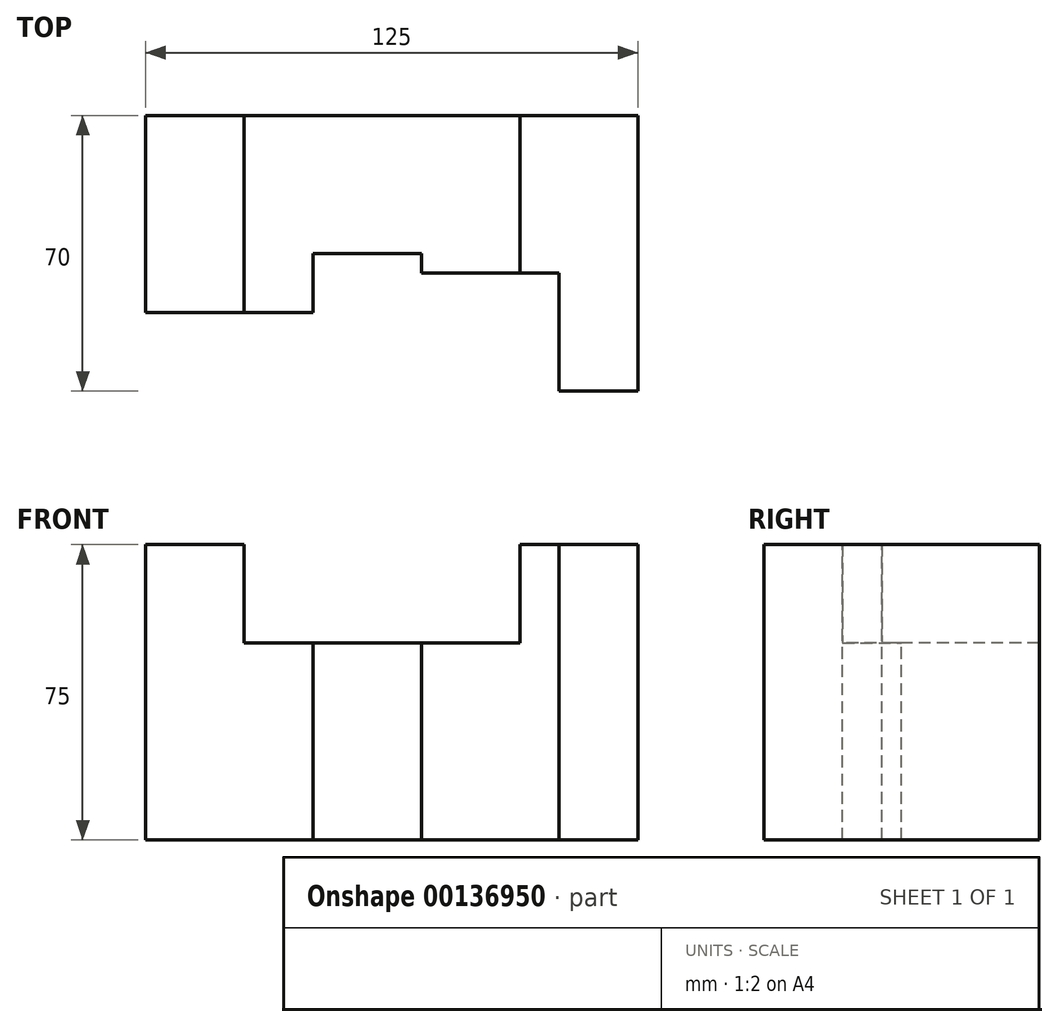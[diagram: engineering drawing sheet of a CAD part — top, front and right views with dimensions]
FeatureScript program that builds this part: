
annotation { "Feature Type Name" : "Feature", "Feature Type Description" : "" }
export const myFeature = defineFeature(function(context is Context, id is Id, definition is map)
    precondition{}
    {
        {
            var Q0;
            Q0=qCreatedBy(makeId("Right.planeOp"),FACE);
            var sketch = newSketch(context, id + "F0", { "sketchPlane" : qUnion([Q0])});
            skLineSegment(sketch, "E0.bottom", {"start": v(0, 0) * mm, "end": v(70, 0) * mm});
            skLineSegment(sketch, "E0.top", {"start": v(0, 75) * mm, "end": v(70, 75) * mm});
            skLineSegment(sketch, "E0.left", {"start": v(0, 0) * mm, "end": v(0, 75) * mm});
            skLineSegment(sketch, "E0.right", {"start": v(70, 0) * mm, "end": v(70, 75) * mm});
            skSolve(sketch);
        }
        {
            var Q0;
            Q0 = qSketchRegion(id + "F0", true);
            extrude(context, id + "F1", {"entities" : qUnion([Q0]), "depth" : 125 * mm});
        }
        {
            var Q0;
            Q0=makeQuery(id+"F1.opExtrude","SWEPT_FACE",FACE,{"disambiguationData":[OSD([sQuery(id+"F0.wireOp",EDGE,"E0.top")])]});
            var sketch = newSketch(context, id + "F2", { "sketchPlane" : qUnion([Q0])});
            skLineSegment(sketch, "E1.0.0", {"start": v(0, 70) * mm, "end": v(0, 0) * mm});
            skLineSegment(sketch, "E1.0.1", {"start": v(0, 0) * mm, "end": v(125, 0) * mm});
            skLineSegment(sketch, "E1.0.2", {"start": v(125, 0) * mm, "end": v(125, 70) * mm});
            skLineSegment(sketch, "E1.0.3", {"start": v(125, 70) * mm, "end": v(0, 70) * mm});
            skLineSegment(sketch, "E2", {"start": v(0, 20) * mm, "end": v(42.5, 20) * mm});
            skLineSegment(sketch, "E3", {"start": v(42.5, 20) * mm, "end": v(42.5, 35) * mm});
            skLineSegment(sketch, "E4", {"start": v(42.5, 35) * mm, "end": v(70, 35) * mm});
            skLineSegment(sketch, "E5", {"start": v(70, 35) * mm, "end": v(70, 30) * mm});
            skLineSegment(sketch, "E6", {"start": v(70, 30) * mm, "end": v(105, 30) * mm});
            skLineSegment(sketch, "E7", {"start": v(105, 30) * mm, "end": v(105, 0) * mm});
            skSolve(sketch);
        }
        {
            var Q0;
            {var subQ0=sQuery(id+"F2.wireOp",EDGE,"E2");Q0=makeQuery(id+"F2.imprint","IMPRINT",FACE,{"disambiguationData":[TD([[makeQuery(id+"F2.imprint","IMPRINT",EDGE,{"derivedFrom":subQ0}),-1.0]])]});}
            extrude(context, id + "F3", {"entities" : qUnion([Q0]), "operationType" : NewBodyOperationType.REMOVE, "endBound" : BoundingType.THROUGH_ALL, "oppositeDirection" : true, "depth" : 25 * mm});
        }
        {
            var Q0;
            Q0=makeQuery(id+"F3.boolean.opBoolean","COPY",FACE,{"derivedFrom":makeQuery(id+"F3.opExtrude","SWEPT_FACE",FACE,{"disambiguationData":[OSD([sQuery(id+"F2.wireOp",EDGE,"E2")])]})});
            var sketch = newSketch(context, id + "F4", { "sketchPlane" : qUnion([Q0])});
            skLineSegment(sketch, "E8.bottom", {"start": v(25, 75) * mm, "end": v(95, 75) * mm});
            skLineSegment(sketch, "E8.top", {"start": v(25, 50) * mm, "end": v(95, 50) * mm});
            skLineSegment(sketch, "E8.left", {"start": v(25, 75) * mm, "end": v(25, 50) * mm});
            skLineSegment(sketch, "E8.right", {"start": v(95, 75) * mm, "end": v(95, 50) * mm});
            skSolve(sketch);
        }
        {
            var Q0;
            Q0 = qSketchRegion(id + "F4", true);
            extrude(context, id + "F5", {"entities" : qUnion([Q0]), "operationType" : NewBodyOperationType.REMOVE, "endBound" : BoundingType.THROUGH_ALL, "oppositeDirection" : true, "depth" : 25 * mm});
        }
    });
